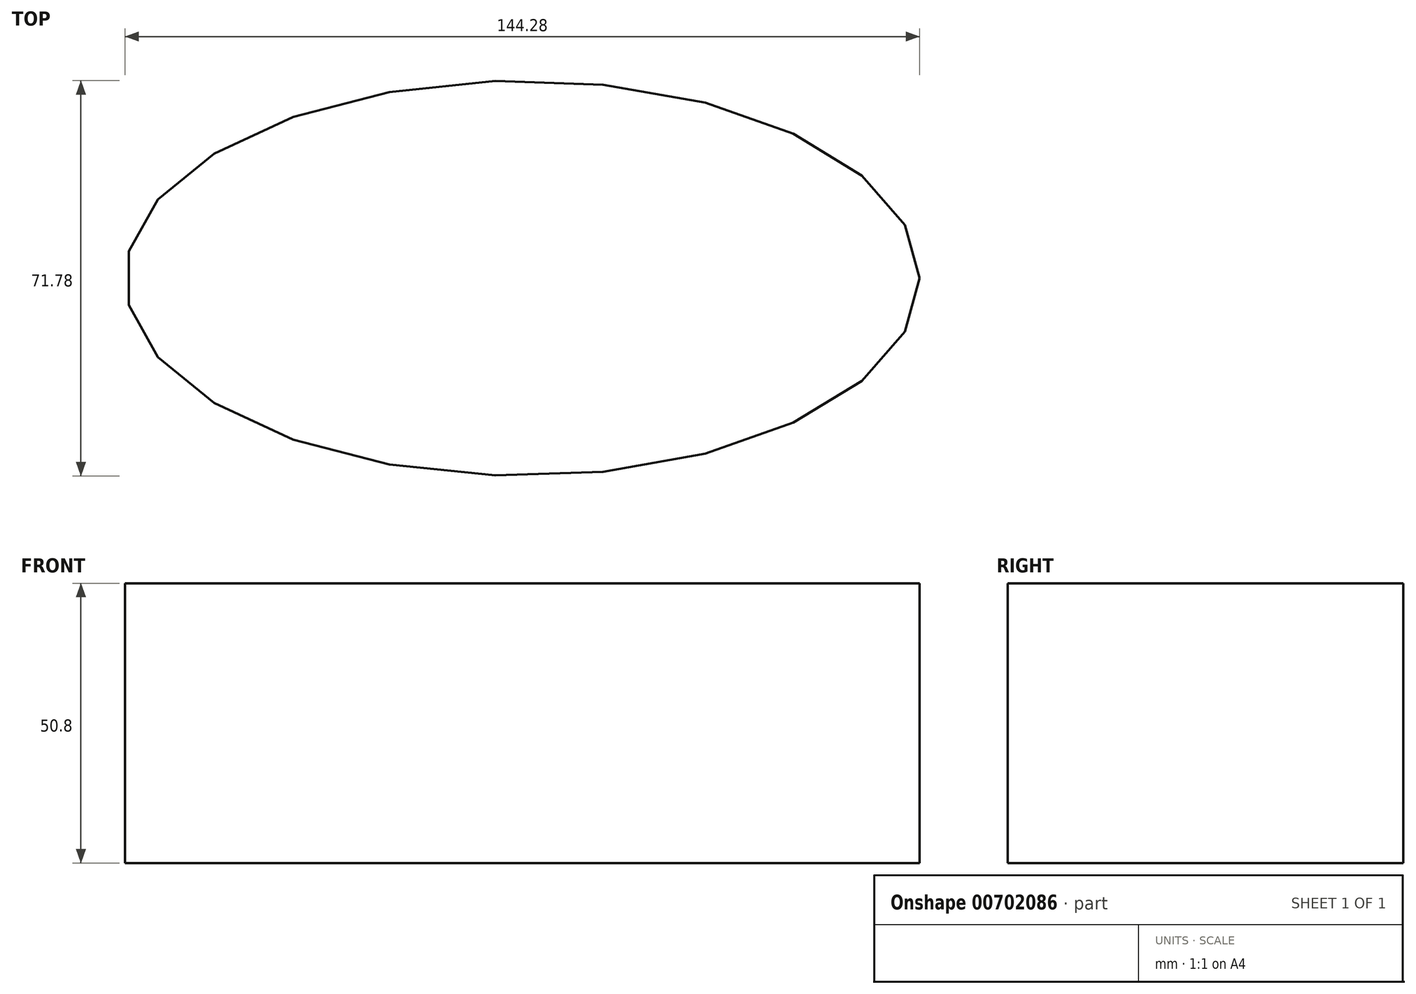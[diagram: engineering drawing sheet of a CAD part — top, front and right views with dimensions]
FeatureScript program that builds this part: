
annotation { "Feature Type Name" : "Feature", "Feature Type Description" : "" }
export const myFeature = defineFeature(function(context is Context, id is Id, definition is map)
    precondition{}
    {
        {
            var Q0;
            Q0=qCreatedBy(makeId("Top.planeOp"),FACE);
            var sketch = newSketch(context, id + "F0", { "sketchPlane" : qUnion([Q0])});
            skEllipse(sketch, "E0", {"center": v(0, 0) * mm, "majorRadius": 72.14 * mm, "minorRadius": 35.9 * mm, "majorAxis": v(1, 0)});
            skSolve(sketch);
        }
        {
            var Q0;
            Q0 = qSketchRegion(id + "F0", true);
            extrude(context, id + "F1", {"entities" : qUnion([Q0]), "depth" : 50.8 * mm, "offsetDistance" : 25.4 * mm});
        }
        {
            var Q0;
            Q0=makeQuery(id+"F1.opExtrude","CAP_FACE",FACE,{"disambiguationData":[OSD([sQuery(id+"F0.wireOp",EDGE,"E0")])],"isStart":false});
            var sketch = newSketch(context, id + "F2", { "sketchPlane" : qUnion([Q0])});
            skSolve(sketch);
        }
        {
            var Q0;
            Q0=makeQuery(id+"F2.imprint","IMPRINT",FACE,{"disambiguationData":[TD([[makeQuery(id+"F2.imprint","IMPRINT",EDGE,{"derivedFrom":makeQuery(id+"F1.opExtrude","CAP_EDGE",EDGE,{"disambiguationData":[OSD([sQuery(id+"F0.wireOp",EDGE,"E0")])],"isStart":false})}),1.0]])]});
            extrude(context, id + "F3", {"entities" : qUnion([Q0]), "operationType" : NewBodyOperationType.ADD, "oppositeDirection" : true, "depth" : 40.83 * mm, "offsetDistance" : 25.4 * mm});
        }
        {
            var Q0;
            Q0=makeQuery(id+"F1.opExtrude","CAP_FACE",FACE,{"disambiguationData":[OSD([sQuery(id+"F0.wireOp",EDGE,"E0")])],"isStart":true});
            var sketch = newSketch(context, id + "F4", { "sketchPlane" : qUnion([Q0])});
            skSolve(sketch);
        }
    });
